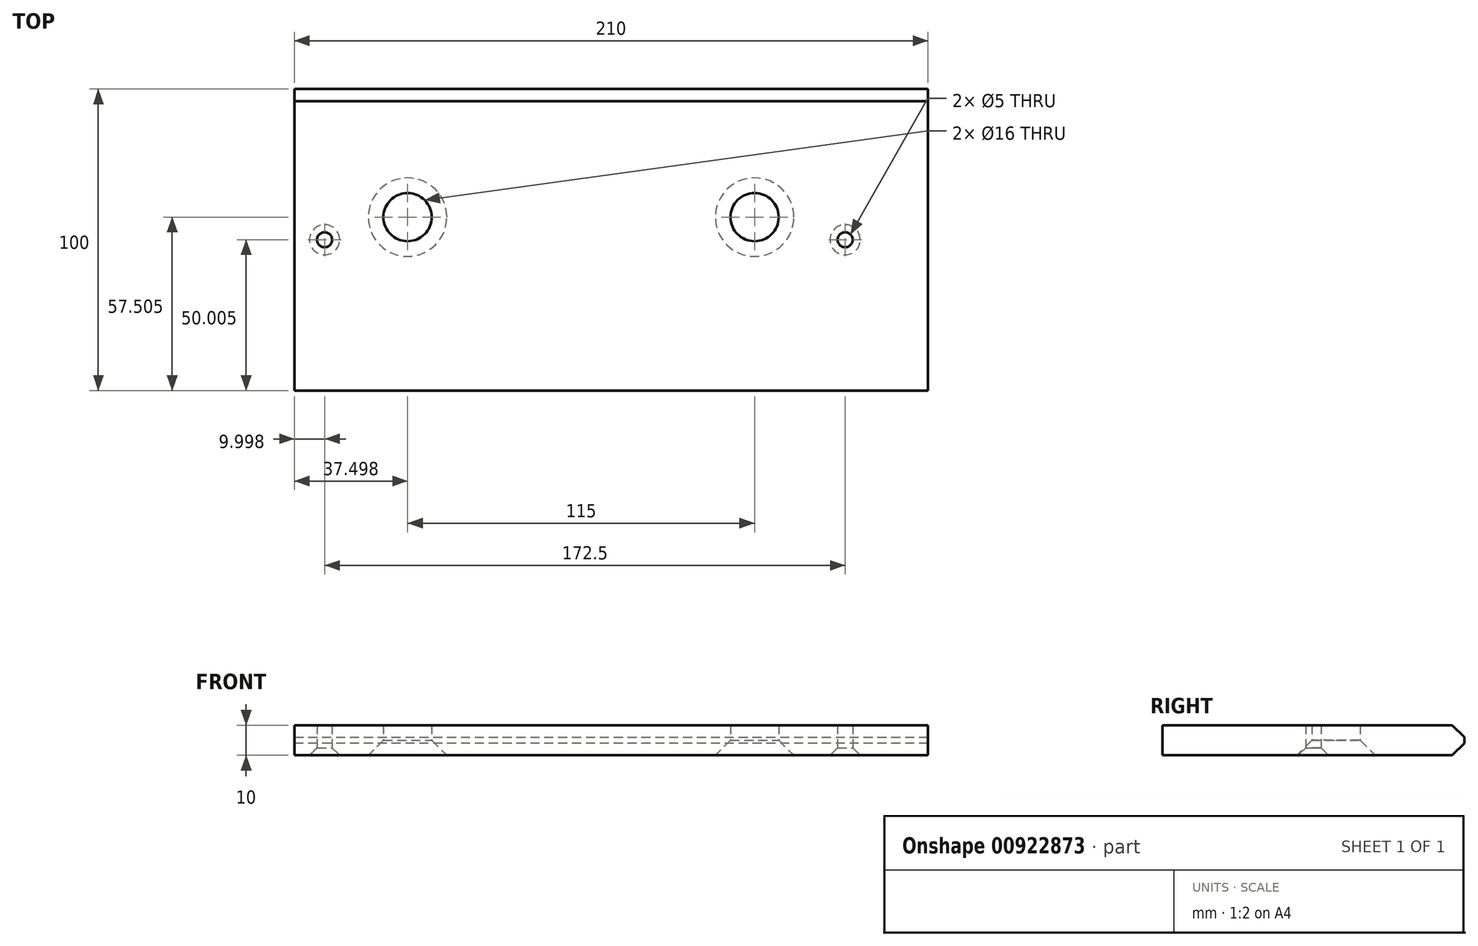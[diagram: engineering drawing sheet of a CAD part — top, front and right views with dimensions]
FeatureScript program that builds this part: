
annotation { "Feature Type Name" : "Feature", "Feature Type Description" : "" }
export const myFeature = defineFeature(function(context is Context, id is Id, definition is map)
    precondition{}
    {
        {
            var Q0;
            Q0=qCreatedBy(makeId("Top.planeOp"),FACE);
            var sketch = newSketch(context, id + "F0", { "sketchPlane" : qUnion([Q0])});
            skLineSegment(sketch, "E0.bottom", {"start": v(-152.43, 94.6) * mm, "end": v(57.57, 94.6) * mm});
            skLineSegment(sketch, "E0.top", {"start": v(-152.43, -5.4) * mm, "end": v(57.57, -5.4) * mm});
            skLineSegment(sketch, "E0.left", {"start": v(-152.43, 94.6) * mm, "end": v(-152.43, -5.4) * mm});
            skLineSegment(sketch, "E0.right", {"start": v(57.57, 94.6) * mm, "end": v(57.57, -5.4) * mm});
            skPoint(sketch, "E1", {"position": v(-142.43, 44.6) * mm});
            skPoint(sketch, "E2", {"position": v(-114.93, 52.1) * mm});
            skPoint(sketch, "E3", {"position": v(0.07, 52.1) * mm});
            skPoint(sketch, "E4", {"position": v(30.07, 44.6) * mm});
            skSolve(sketch);
        }
        {
            var Q0;
            Q0 = qSketchRegion(id + "F0", true);
            extrude(context, id + "F1", {"entities" : qUnion([Q0]), "depth" : 10 * mm, "offsetDistance" : 25 * mm});
        }
        {
            var Q0;
            Q0=sQuery(id+"F0.wireOp",VERTEX,"E4");
            var Q1;
            Q1=sQuery(id+"F0.wireOp",VERTEX,"E1");
            var Q2;
            Q2=makeQuery(id+"F1.opExtrude","SWEPT_BODY",BODY,{"disambiguationData":[OSD([sQuery(id+"F0.wireOp",EDGE,"E0.bottom"),sQuery(id+"F0.wireOp",EDGE,"E0.top"),sQuery(id+"F0.wireOp",EDGE,"E0.left"),sQuery(id+"F0.wireOp",EDGE,"E0.right")])]});
            hole(context, id + "F2", {"style" : HoleStyle.C_SINK, "endStyle" : HoleEndStyle.THROUGH, "oppositeDirection" : true, "holeDiameter" : 5 * mm, "cSinkDiameter" : 10 * mm, "cSinkAngle" : 90 * degree, "majorDiameter" : 5 * mm, "isTappedThrough" : true, "tappedDepth" : 12 * mm, "tapClearance" : 3, "startFromSketch" : true, "locations" : qUnion([Q0, Q1]), "scope" : qUnion([Q2])});
        }
        {
            var Q0;
            Q0=sQuery(id+"F0.wireOp",VERTEX,"E2");
            var Q1;
            Q1=sQuery(id+"F0.wireOp",VERTEX,"E3");
            var Q2;
            Q2=makeQuery(id+"F1.opExtrude","SWEPT_BODY",BODY,{"disambiguationData":[OSD([sQuery(id+"F0.wireOp",EDGE,"E0.bottom"),sQuery(id+"F0.wireOp",EDGE,"E0.top"),sQuery(id+"F0.wireOp",EDGE,"E0.left"),sQuery(id+"F0.wireOp",EDGE,"E0.right")])]});
            hole(context, id + "F3", {"style" : HoleStyle.C_SINK, "endStyle" : HoleEndStyle.THROUGH, "oppositeDirection" : true, "holeDiameter" : 16 * mm, "cSinkDiameter" : 26 * mm, "cSinkAngle" : 90 * degree, "majorDiameter" : 5 * mm, "isTappedThrough" : true, "tappedDepth" : 12 * mm, "tapClearance" : 3, "startFromSketch" : true, "locations" : qUnion([Q0, Q1]), "scope" : qUnion([Q2])});
        }
        {
            var Q0;
            Q0=makeQuery(id+"F1.opExtrude","CAP_EDGE",EDGE,{"disambiguationData":[OSD([sQuery(id+"F0.wireOp",EDGE,"E0.bottom")])],"isStart":true});
            var Q1;
            Q1=makeQuery(id+"F1.opExtrude","CAP_EDGE",EDGE,{"disambiguationData":[OSD([sQuery(id+"F0.wireOp",EDGE,"E0.bottom")])],"isStart":false});
            chamfer(context, id + "F4", {"entities" : qUnion([Q0, Q1]), "width" : 4 * mm, "tangentPropagation" : true});
        }
    });
